# Revit family: Faucet-Lavatory-Spout-KOHLER-ARTIFACTS-K-72758T_1
name_source: partatom
category: Plumbing Fixtures
units: mm (PartAtom-declared; Revit-internal decimal feet)

## family parameters
Cut with Voids When Loaded = No
Host = Face
OmniClass Number = 23.31.11.00
OmniClass Title = Faucets
Part Type = Normal
Room Calculation Point = No
Round Connector Dimension = Use Diameter
Shared = No

## types (15) — shared parameters
ADA Compliant = No
Assembly Code = D2010
CW Connection = No
Cold Water Inlet = Cold Water Inlet
Date Modified = 06/01/2023
Default Elevation = 36"
Drain Included = Yes
HW Connection = Yes
Height = 4 11/16"
Hot Water Inlet = Hot Water Inlet
Length = 5 3/8"
Manufacturer = Kohler Co.
Master Format 2014 = 22 41 39
Master Format 2014 Name = Residential Faucets, Supplies, and Trim
Material = Premium Metal Construction
Pressure = 0.00 psi
Product Name = Artifacts
Spout Reach = 5 3/8"
Tempered Water Inlet = Tempered Water Inlet
URL = http://www.kohler.com.cn
Vent Connection = No
Waste Connection = No
Waste Water Outlet = Waste Water Outlet
WaterSense Certified = No
Width = 3 1/8"

## per-type parameters (varying)
| type | Description | Finish | Flow Rate | Model | Product Documentation Link | Product Page URL | Type |
| 2.2 GPM, CP-Polished Chrome | 8 inch basin tap out of the mouth curved outlet | Kohler-Metal-CP-Polished_Chrome | 2 GPM | K-72758T-CP | https://files.kohler.com.cn | https://www.kohler.com.cn | 1 |
| 2.2 GPM, BV-Brushed Bronze | 8 inch basin tap out of the mouth curved outlet | Kohler-Metal-BV-Brushed_Bronze | 2 GPM | K-72758T-BV | https://files.kohler.com.cn | https://www.kohler.com.cn | 2 |
| 2.2 GPM, RGD-Polished Rose Gold | 8 inch basin tap out of the mouth curved outlet | Kohler-Metal-RGD-Polished_Rose_Gold | 2 GPM | K-72758T-RGD | https://files.kohler.com.cn | https://www.kohler.com.cn | 3 |
| 2.2 GPM, 2BZ-Oil Rubbed Bronze | 8 inch basin tap out of the mouth curved outlet | Kohler-Metal-2BZ-Oil_Rubbed_Bronze | 2 GPM | K-72758T-2BZ | https://files.kohler.com.cn | https://www.kohler.com.cn | 4 |
| 2.2 GPM, AF-Vibrant French Gold | 8 inch basin tap out of the mouth curved outlet | Kohler-Metal-AF-Vibrant_French_Gold | 2 GPM | K-72758T-AF | https://files.kohler.com.cn | https://www.kohler.com.cn | 5 |
| 2.2 GPM, BN-Vibrant Brushed Nickel | 8 inch basin tap out of the mouth curved outlet | Kohler-Metal-BN-Vibrant_Brushed_Nickel | 2 GPM | K-72758T-BN | https://files.kohler.com.cn | https://www.kohler.com.cn | 6 |
| 2.2 GPM, SN-Vibrant Polished Nickel | 8 inch basin tap out of the mouth curved outlet | Kohler-Metal-SN-Vibrant_Polished_Nickel | 2 GPM | K-72758T-SN | https://files.kohler.com.cn | https://www.kohler.com.cn | 7 |
| 2.2 GPM, PGD-Modern Polished Gold | 8 inch basin tap out of the mouth curved outlet | Kohler-Metal-PGD-Modern_Polished_Gold | 2 GPM | K-72758T-PGD | https://files.kohler.com.cn | https://www.kohler.com.cn | 8 |
| 2.2 GPM, TT-Vibrant Titanium | 8 inch basin tap out of the mouth curved outlet | Kohler-Metal-TT-Vibrant_Titanium | 2 GPM | K-72758T-TT | https://files.kohler.com.cn | https://www.kohler.com.cn | 9 |
| 2.2 GPM, 2BL-Black | 8 inch basin tap out of the mouth curved outlet | KOHLER-Metal-2BL-Black | 2 GPM | K-72758T-2BL | https://files.kohler.com.cn | https://www.kohler.com.cn | 10 |
| 1.0 GPM, 2BZ-Oil Rubbed Bronze | Lavatory Spout - TEA | Kohler-Metal-2BZ-Oil_Rubbed_Bronze | 1 GPM | K-72758T-E2-2BZ |  |  | 11 |
| 1.0 GPM, AF-Vibrant French Gold | Lavatory Spout - TEA | Kohler-Metal-AF-Vibrant_French_Gold | 1 GPM | K-72758T-E2-AF |  |  | 12 |
| 1.0 GPM, BN-Vibrant Brushed Nickel | Lavatory Spout - TEA | Kohler-Metal-BN-Vibrant_Brushed_Nickel | 1 GPM | K-72758T-E2-BN |  |  | 13 |
| 1.0 GPM, BV-Brushed Bronze | Lavatory Spout - TEA | Kohler-Metal-BV-Brushed_Bronze | 1 GPM | K-72758T-E2-BV |  |  | 14 |
| 1.0 GPM, CP-Polished Chrome | Lavatory Spout - TEA | Kohler-Metal-CP-Polished_Chrome | 1 GPM | K-72758T-E2-CP |  |  | 15 |

## geometry (parser evidence)
native form markers: Sweep x3
no freeform markers — native parametric forms only
